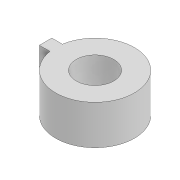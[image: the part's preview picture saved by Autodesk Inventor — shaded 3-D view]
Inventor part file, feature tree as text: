
AUTODESK INVENTOR PART (.ipt)
format: ipt  version: 2022 (Build 260153000, 153)  size: 88,064 bytes
history: native  units: mm
features: extrude x1, sketch x1
ambient origin geometry x8: Origin, YZ Plane, XZ Plane, XY Plane, X Axis, Y Axis, Z Axis, Center Point
bodies: Solid1 (feature_tree)
feature tree (2):
  extrude  "Extrusion1"  Depth=10.0mm
  sketch  "Sketch1"  dims[d0=20.0mm d1=9.534878mm d2=10.0mm d3=0.0mm]
